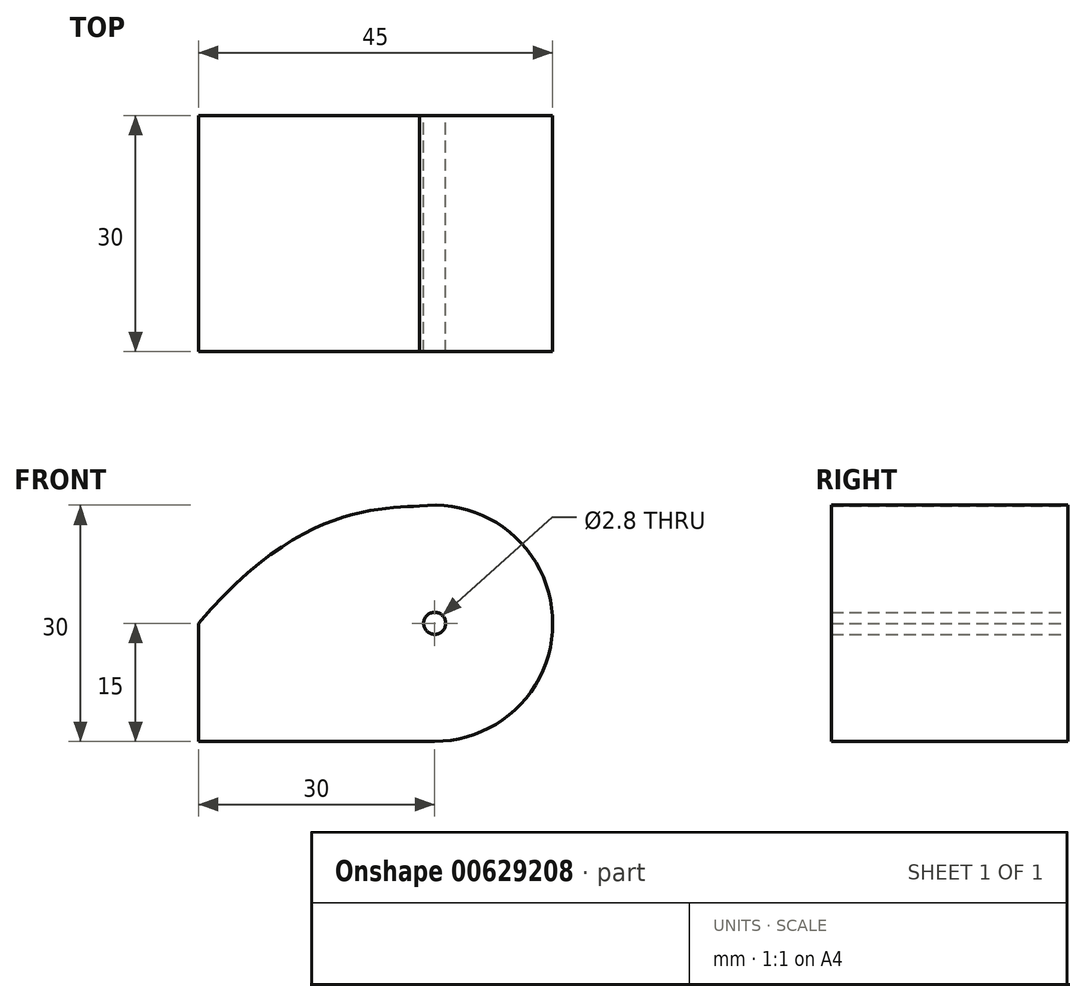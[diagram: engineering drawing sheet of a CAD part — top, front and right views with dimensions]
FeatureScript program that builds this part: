
annotation { "Feature Type Name" : "Feature", "Feature Type Description" : "" }
export const myFeature = defineFeature(function(context is Context, id is Id, definition is map)
    precondition{}
    {
        {
            var Q0;
            Q0=qCreatedBy(makeId("Front.planeOp"),FACE);
            var sketch = newSketch(context, id + "F0", { "sketchPlane" : qUnion([Q0])});
            skArc(sketch, "E0", {"start": v(0, -15) * mm, "mid": v(14.97, 0.96) * mm, "end": v(-1.92, 14.88) * mm});
            skLineSegment(sketch, "E1.top", {"start": v(0, -15) * mm, "end": v(-30, -15) * mm});
            skLineSegment(sketch, "E1.right", {"start": v(-30, 0) * mm, "end": v(-30, -15) * mm});
            skFitSpline(sketch, "E2", {"points": [v(-30, 0) * mm, v(0, 15) * mm], "startDerivative": vector(41.74, 49.62) * mm, "endDerivative": vector(14.58, 1.72) * mm});
            skCircle(sketch, "E3", {"center": v(0, 0) * mm, "radius": 1.4 * mm});
            skSolve(sketch);
        }
        {
            var Q0;
            Q0 = qSketchRegion(id + "F0", true);
            extrude(context, id + "F1", {"entities" : qUnion([Q0]), "depth" : 30 * mm, "offsetDistance" : 25.4 * mm});
        }
    });
